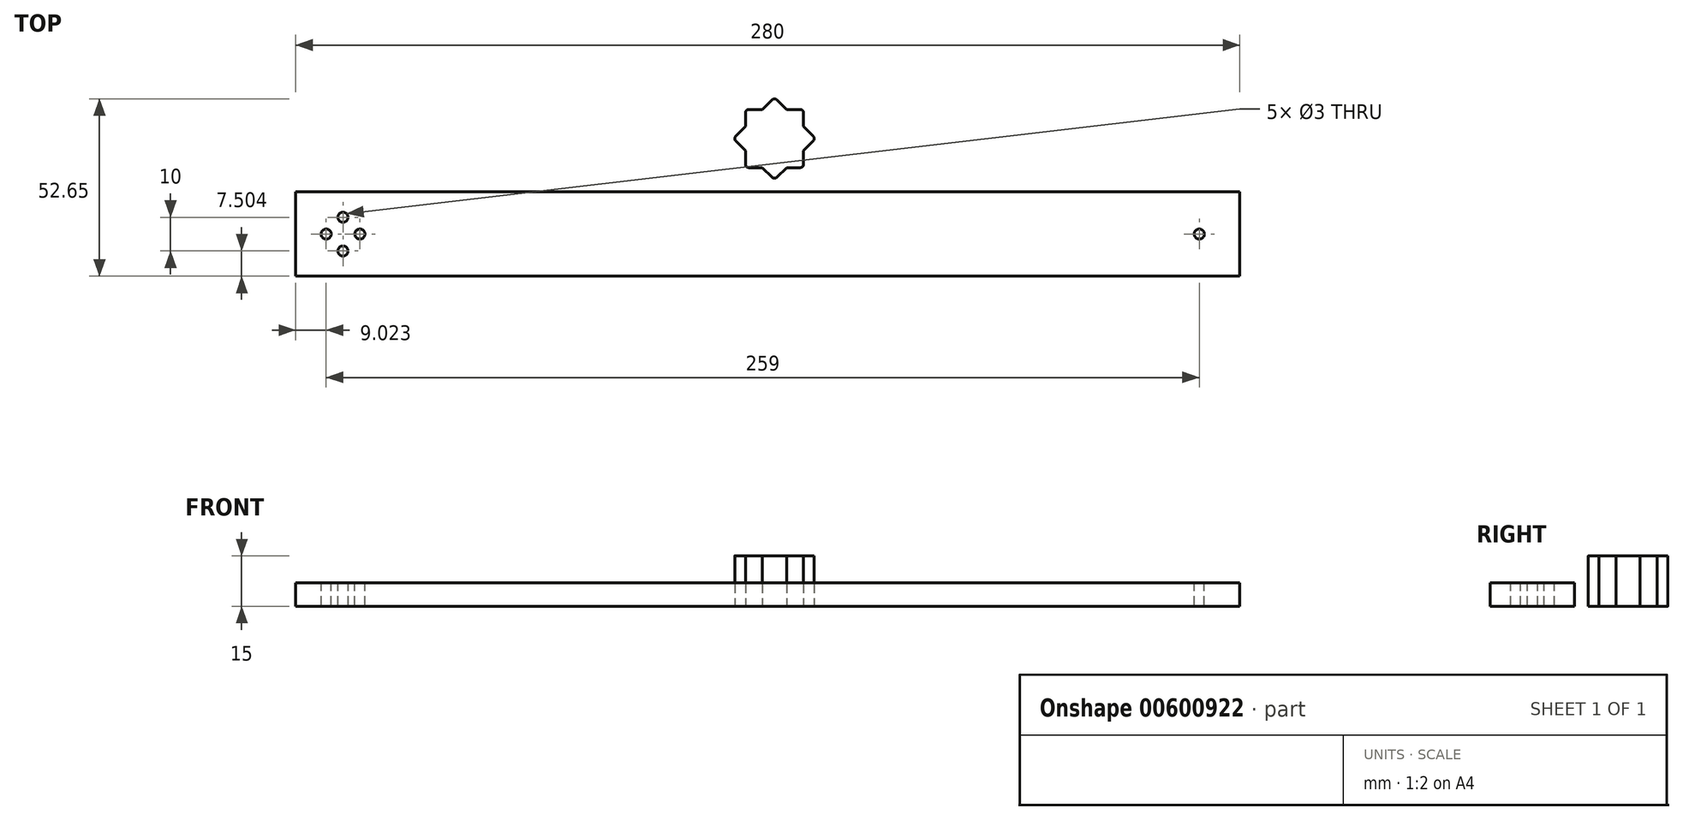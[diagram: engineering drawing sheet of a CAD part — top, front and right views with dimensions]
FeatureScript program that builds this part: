
annotation { "Feature Type Name" : "Feature", "Feature Type Description" : "" }
export const myFeature = defineFeature(function(context is Context, id is Id, definition is map)
    precondition{}
    {
        {
            var Q0;
            Q0=qCreatedBy(makeId("Top.planeOp"),FACE);
            var sketch = newSketch(context, id + "F0", { "sketchPlane" : qUnion([Q0])});
            skLineSegment(sketch, "E0.bottom", {"start": v(-8.63, 8.63) * mm, "end": v(8.63, 8.63) * mm});
            skLineSegment(sketch, "E0.top", {"start": v(-8.63, -8.63) * mm, "end": v(8.63, -8.63) * mm});
            skLineSegment(sketch, "E0.left", {"start": v(-8.63, 8.63) * mm, "end": v(-8.63, -8.63) * mm});
            skLineSegment(sketch, "E0.right", {"start": v(8.63, 8.63) * mm, "end": v(8.63, -8.63) * mm});
            skLineSegment(sketch, "E1", {"start": v(0, 12.2) * mm, "end": v(12.2, 0) * mm});
            skLineSegment(sketch, "E2", {"start": v(12.2, 0) * mm, "end": v(0, -12.2) * mm});
            skLineSegment(sketch, "E3", {"start": v(0, -12.2) * mm, "end": v(-12.2, 0) * mm});
            skLineSegment(sketch, "E4", {"start": v(-12.2, 0) * mm, "end": v(0, 12.2) * mm});
            skSolve(sketch);
        }
        {
            var Q0;
            Q0 = qSketchRegion(id + "F0", true);
            extrude(context, id + "F1", {"entities" : qUnion([Q0]), "depth" : 15 * mm, "offsetDistance" : 25 * mm});
        }
        {
            var Q0;
            Q0=makeQuery(id+"F1.opExtrude","CAP_FACE",FACE,{"disambiguationData":[OSD([sQuery(id+"F0.wireOp",EDGE,"E0.bottom"),sQuery(id+"F0.wireOp",EDGE,"E0.top"),sQuery(id+"F0.wireOp",EDGE,"E0.left"),sQuery(id+"F0.wireOp",EDGE,"E0.right"),sQuery(id+"F0.wireOp",EDGE,"E1"),sQuery(id+"F0.wireOp",EDGE,"E2"),sQuery(id+"F0.wireOp",EDGE,"E3"),sQuery(id+"F0.wireOp",EDGE,"E4")])],"isStart":false});
            var sketch = newSketch(context, id + "F2", { "sketchPlane" : qUnion([Q0])});
            skCircle(sketch, "E5", {"center": v(0, 0) * mm, "radius": 5 * mm, "construction": true});
            skCircle(sketch, "E6", {"center": v(0, 0) * mm, "radius": 7.5 * mm, "construction": true});
            skArc(sketch, "E7", {"start": v(0, 5) * mm, "mid": v(3.54, 3.54) * mm, "end": v(5, 0) * mm});
            skArc(sketch, "E8", {"start": v(0, 7.5) * mm, "mid": v(5.3, 5.3) * mm, "end": v(7.5, 0) * mm});
            skArc(sketch, "E9", {"start": v(5, 0) * mm, "mid": v(6.25, -1.25) * mm, "end": v(7.5, 0) * mm});
            skArc(sketch, "E10", {"start": v(0, 5) * mm, "mid": v(-1.25, 6.25) * mm, "end": v(0, 7.5) * mm});
            skSolve(sketch);
        }
        {
            var Q0;
            Q0=qCreatedBy(makeId("Right.planeOp"),FACE);
            var sketch = newSketch(context, id + "F3", { "sketchPlane" : qUnion([Q0])});
            skLineSegment(sketch, "E11", {"start": v(0, 50.49) * mm, "end": v(0, -51.14) * mm, "construction": true});
            skSolve(sketch);
        }
        {
            var Q0;
            Q0=makeQuery(id+"F1.opExtrude","SWEPT_EDGE",EDGE,{"disambiguationData":[OSD([sQuery(id+"F0.wireOp",EDGE,"E0.bottom"),sQuery(id+"F0.wireOp",EDGE,"E0.right")])]});
            var Q1;
            Q1=makeQuery(id+"F1.opExtrude","SWEPT_EDGE",EDGE,{"disambiguationData":[OSD([sQuery(id+"F0.wireOp",EDGE,"E0.bottom"),sQuery(id+"F0.wireOp",EDGE,"E0.left")])]});
            var Q2;
            Q2=makeQuery(id+"F1.opExtrude","SWEPT_EDGE",EDGE,{"disambiguationData":[OSD([sQuery(id+"F0.wireOp",EDGE,"E1"),sQuery(id+"F0.wireOp",EDGE,"E2")])]});
            var Q3;
            Q3=makeQuery(id+"F1.opExtrude","SWEPT_EDGE",EDGE,{"disambiguationData":[OSD([sQuery(id+"F0.wireOp",EDGE,"E0.top"),sQuery(id+"F0.wireOp",EDGE,"E0.right")])]});
            var Q4;
            Q4=makeQuery(id+"F1.opExtrude","SWEPT_EDGE",EDGE,{"disambiguationData":[OSD([sQuery(id+"F0.wireOp",EDGE,"E2"),sQuery(id+"F0.wireOp",EDGE,"E3")])]});
            var Q5;
            Q5=makeQuery(id+"F1.opExtrude","SWEPT_EDGE",EDGE,{"disambiguationData":[OSD([sQuery(id+"F0.wireOp",EDGE,"E3"),sQuery(id+"F0.wireOp",EDGE,"E4")])]});
            var Q6;
            Q6=makeQuery(id+"F1.opExtrude","SWEPT_EDGE",EDGE,{"disambiguationData":[OSD([sQuery(id+"F0.wireOp",EDGE,"E0.top"),sQuery(id+"F0.wireOp",EDGE,"E0.left")])]});
            var Q7;
            Q7=makeQuery(id+"F1.opExtrude","SWEPT_EDGE",EDGE,{"disambiguationData":[OSD([sQuery(id+"F0.wireOp",EDGE,"E1"),sQuery(id+"F0.wireOp",EDGE,"E4")])]});
            fillet(context, id + "F4", {"entities" : qUnion([Q0, Q1, Q2, Q3, Q4, Q5, Q6, Q7]), "radius" : 1 * mm, "tangentPropagation" : true, "allowEdgeOverflow" : false});
        }
        {
            var Q0;
            Q0=qCreatedBy(makeId("Top.planeOp"),FACE);
            var sketch = newSketch(context, id + "F5", { "sketchPlane" : qUnion([Q0])});
            skLineSegment(sketch, "E12.bottom", {"start": v(-142.01, -15.86) * mm, "end": v(137.99, -15.86) * mm});
            skLineSegment(sketch, "E12.top", {"start": v(-142.01, -40.86) * mm, "end": v(137.99, -40.86) * mm});
            skLineSegment(sketch, "E12.left", {"start": v(-142.01, -15.86) * mm, "end": v(-142.01, -40.86) * mm});
            skLineSegment(sketch, "E12.right", {"start": v(137.99, -15.86) * mm, "end": v(137.99, -40.86) * mm});
            skLineSegment(sketch, "E13", {"start": v(-142.01, -28.36) * mm, "end": v(154.75, -28.36) * mm, "construction": true});
            skSolve(sketch);
        }
        {
            var Q0;
            Q0=makeQuery(id+"F5.imprint","IMPRINT",FACE,{"disambiguationData":[TD([[makeQuery(id+"F5.imprint","IMPRINT",EDGE,{"derivedFrom":sQuery(id+"F5.wireOp",EDGE,"E12.bottom")}),-1.0]])]});
            extrude(context, id + "F6", {"entities" : qUnion([Q0]), "depth" : 7 * mm, "offsetDistance" : 25 * mm});
        }
        {
            var Q0;
            Q0=makeQuery(id+"F1.opExtrude","CAP_FACE",FACE,{"disambiguationData":[OSD([sQuery(id+"F0.wireOp",EDGE,"E0.bottom"),sQuery(id+"F0.wireOp",EDGE,"E0.top"),sQuery(id+"F0.wireOp",EDGE,"E0.left"),sQuery(id+"F0.wireOp",EDGE,"E0.right"),sQuery(id+"F0.wireOp",EDGE,"E1"),sQuery(id+"F0.wireOp",EDGE,"E2"),sQuery(id+"F0.wireOp",EDGE,"E3"),sQuery(id+"F0.wireOp",EDGE,"E4")])],"isStart":false});
            var sketch = newSketch(context, id + "F7", { "sketchPlane" : qUnion([Q0])});
            skCircle(sketch, "E14", {"center": v(-5, 0) * mm, "radius": 1.5 * mm});
            skSolve(sketch);
        }
        {
            var Q0;
            Q0=makeQuery(id+"F6.opExtrude","CAP_FACE",FACE,{"disambiguationData":[OSD([sQuery(id+"F5.wireOp",EDGE,"E12.bottom"),sQuery(id+"F5.wireOp",EDGE,"E12.top"),sQuery(id+"F5.wireOp",EDGE,"E12.left"),sQuery(id+"F5.wireOp",EDGE,"E12.right")])],"isStart":false});
            var sketch = newSketch(context, id + "F8", { "sketchPlane" : qUnion([Q0])});
            skLineSegment(sketch, "E15", {"start": v(-127.99, -52.24) * mm, "end": v(-127.99, -9.5) * mm, "construction": true});
            skLineSegment(sketch, "E16", {"start": v(-142.01, -28.36) * mm, "end": v(154.53, -28.36) * mm, "construction": true});
            skCircle(sketch, "E17", {"center": v(-127.99, -23.36) * mm, "radius": 1.5 * mm});
            skCircle(sketch, "E18", {"center": v(-132.99, -28.36) * mm, "radius": 1.5 * mm});
            skCircle(sketch, "E19", {"center": v(-122.99, -28.36) * mm, "radius": 1.5 * mm});
            skCircle(sketch, "E20", {"center": v(-127.99, -33.36) * mm, "radius": 1.5 * mm});
            skCircle(sketch, "E21", {"center": v(126.01, -28.36) * mm, "radius": 1.5 * mm});
            skSolve(sketch);
        }
        {
            var Q0;
            Q0 = qSketchRegion(id + "F8", true);
            extrude(context, id + "F9", {"entities" : qUnion([Q0]), "operationType" : NewBodyOperationType.REMOVE, "endBound" : BoundingType.UP_TO_NEXT, "oppositeDirection" : true, "depth" : 25 * mm, "offsetDistance" : 25 * mm});
        }
    });
